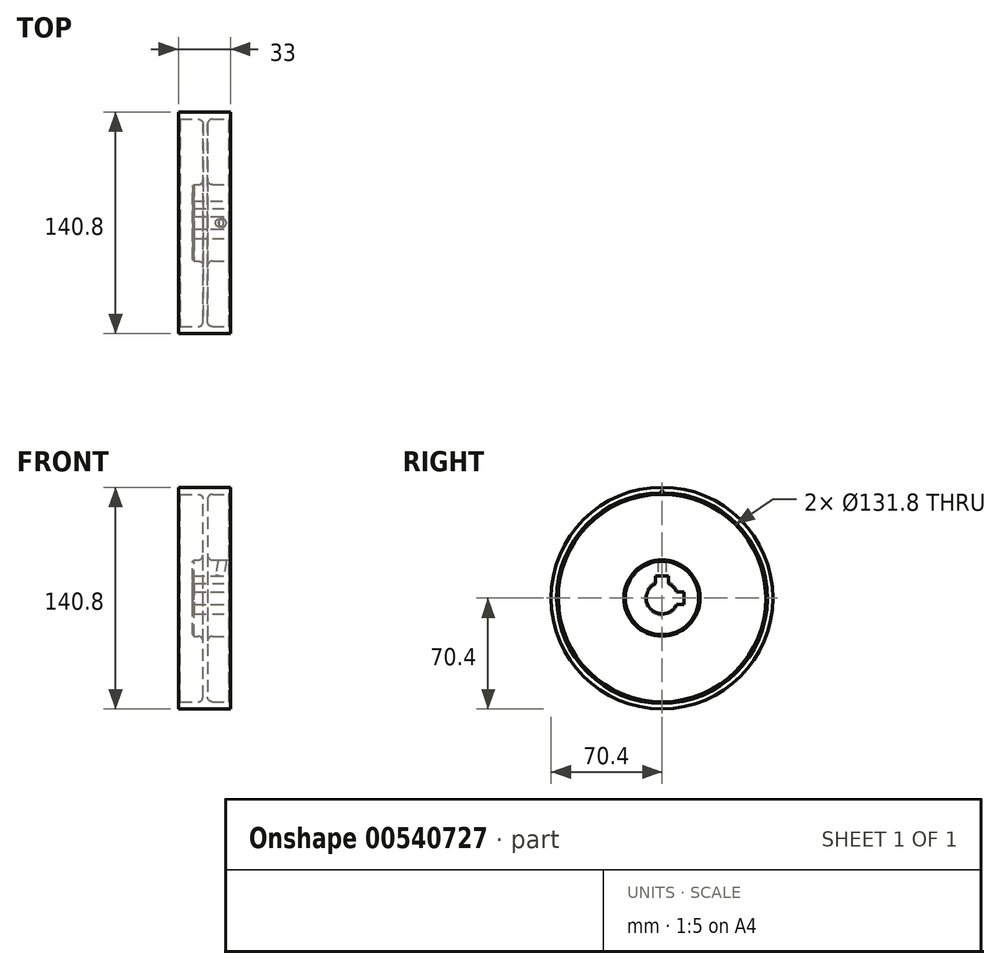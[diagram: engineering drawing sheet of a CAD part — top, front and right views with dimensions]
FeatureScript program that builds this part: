
annotation { "Feature Type Name" : "Feature", "Feature Type Description" : "" }
export const myFeature = defineFeature(function(context is Context, id is Id, definition is map)
    precondition{}
    {
        {
            var Q0;
            Q0=qCreatedBy(makeId("Front.planeOp"),FACE);
            var sketch = newSketch(context, id + "F0", { "sketchPlane" : qUnion([Q0])});
            skLineSegment(sketch, "E0", {"start": v(-11.99, 0) * mm, "end": v(-11.99, 24.25) * mm});
            skLineSegment(sketch, "E1", {"start": v(-11.99, 24.25) * mm, "end": v(-5.49, 24.25) * mm});
            skLineSegment(sketch, "E2", {"start": v(-5.49, 24.25) * mm, "end": v(-5.49, 65.9) * mm});
            skLineSegment(sketch, "E3", {"start": v(-5.49, 65.9) * mm, "end": v(-20.99, 65.9) * mm});
            skLineSegment(sketch, "E4", {"start": v(-20.99, 65.9) * mm, "end": v(-20.99, 70.4) * mm});
            skLineSegment(sketch, "E5", {"start": v(-20.99, 70.4) * mm, "end": v(12.01, 70.4) * mm});
            skLineSegment(sketch, "E6", {"start": v(12.01, 70.4) * mm, "end": v(12.01, 65.9) * mm});
            skLineSegment(sketch, "E7", {"start": v(12.01, 65.9) * mm, "end": v(-2.49, 65.9) * mm});
            skLineSegment(sketch, "E8", {"start": v(-2.49, 65.9) * mm, "end": v(-2.49, 24.25) * mm});
            skLineSegment(sketch, "E9", {"start": v(-2.49, 24.25) * mm, "end": v(12.01, 24.25) * mm});
            skLineSegment(sketch, "E10", {"start": v(12.01, 24.25) * mm, "end": v(12.01, 0) * mm});
            skLineSegment(sketch, "E11", {"start": v(0, 0) * mm, "end": v(-51.76, 0) * mm, "construction": true});
            skLineSegment(sketch, "E12", {"start": v(-11.99, 0) * mm, "end": v(12.01, 0) * mm});
            skSolve(sketch);
        }
        {
            var Q0;
            Q0=makeQuery(id+"F0.imprint","IMPRINT",FACE,{"disambiguationData":[TD([[makeQuery(id+"F0.imprint","IMPRINT",EDGE,{"derivedFrom":sQuery(id+"F0.wireOp",EDGE,"E0")}),-1.0]])]});
            var Q1;
            Q1=sQuery(id+"F0.wireOp",EDGE,"E11");
            revolve(context, id + "F1", {"surfaceOperationType" : NewSurfaceOperationType.NEW, "entities" : qUnion([Q0]), "axis" : qUnion([Q1]), "revolveType" : RevolveType.FULL});
        }
        {
            var Q0;
            Q0=makeQuery(id+"F1.opRevolve","SWEPT_EDGE",EDGE,{"disambiguationData":[OSD([sQuery(id+"F0.wireOp",EDGE,"E8"),sQuery(id+"F0.wireOp",EDGE,"E9")])]});
            var Q1;
            Q1=makeQuery(id+"F1.opRevolve","SWEPT_EDGE",EDGE,{"disambiguationData":[OSD([sQuery(id+"F0.wireOp",EDGE,"E7"),sQuery(id+"F0.wireOp",EDGE,"E8")])]});
            var Q2;
            Q2=makeQuery(id+"F1.opRevolve","SWEPT_EDGE",EDGE,{"disambiguationData":[OSD([sQuery(id+"F0.wireOp",EDGE,"E1"),sQuery(id+"F0.wireOp",EDGE,"E2")])]});
            var Q3;
            Q3=makeQuery(id+"F1.opRevolve","SWEPT_EDGE",EDGE,{"disambiguationData":[OSD([sQuery(id+"F0.wireOp",EDGE,"E2"),sQuery(id+"F0.wireOp",EDGE,"E3")])]});
            fillet(context, id + "F2", {"entities" : qUnion([Q0, Q1, Q2, Q3]), "radius" : 3 * mm, "tangentPropagation" : true, "allowEdgeOverflow" : false});
        }
        {
            var Q0;
            Q0=makeQuery(id+"F1.opRevolve","SWEPT_FACE",FACE,{"disambiguationData":[OSD([sQuery(id+"F0.wireOp",EDGE,"E10")])]});
            var sketch = newSketch(context, id + "F3", { "sketchPlane" : qUnion([Q0])});
            skArc(sketch, "E13", {"start": v(-4, 9.17) * mm, "mid": v(-7.07, -7.07) * mm, "end": v(9.17, -4) * mm});
            skLineSegment(sketch, "E14.bottom", {"start": v(4, 14) * mm, "end": v(-4, 14) * mm});
            skLineSegment(sketch, "E14.left", {"start": v(4, 14) * mm, "end": v(4, 9.17) * mm});
            skLineSegment(sketch, "E14.right", {"start": v(-4, 14) * mm, "end": v(-4, 9.17) * mm});
            skPoint(sketch, "E14.middle", {"position": v(0, 10) * mm});
            skLineSegment(sketch, "E15.bottom", {"start": v(14, -4) * mm, "end": v(9.17, -4) * mm});
            skLineSegment(sketch, "E15.top", {"start": v(14, 4) * mm, "end": v(9.17, 4) * mm});
            skLineSegment(sketch, "E15.left", {"start": v(14, -4) * mm, "end": v(14, 4) * mm});
            skPoint(sketch, "E15.middle", {"position": v(10, 0) * mm});
            skArc(sketch, "E16.trimOffspring", {"start": v(9.17, 4) * mm, "mid": v(7.07, 7.07) * mm, "end": v(4, 9.17) * mm});
            skSolve(sketch);
        }
        {
            var Q0;
            Q0=makeQuery(id+"F3.imprint","IMPRINT",FACE,{"disambiguationData":[TD([[makeQuery(id+"F3.imprint","IMPRINT",EDGE,{"derivedFrom":sQuery(id+"F3.wireOp",EDGE,"E13")}),1.0]])]});
            extrude(context, id + "F4", {"entities" : qUnion([Q0]), "operationType" : NewBodyOperationType.REMOVE, "oppositeDirection" : true, "depth" : 25 * mm, "offsetDistance" : 25 * mm});
        }
        {
            var Q0;
            Q0=makeQuery(id+"F1.opRevolve","SWEPT_EDGE",EDGE,{"disambiguationData":[OSD([sQuery(id+"F0.wireOp",EDGE,"E6"),sQuery(id+"F0.wireOp",EDGE,"E7")])]});
            var Q1;
            Q1=makeQuery(id+"F1.opRevolve","SWEPT_EDGE",EDGE,{"disambiguationData":[OSD([sQuery(id+"F0.wireOp",EDGE,"E9"),sQuery(id+"F0.wireOp",EDGE,"E10")])]});
            var Q2;
            Q2=makeQuery(id+"F4.boolean.opBoolean","COPY",EDGE,{"derivedFrom":makeQuery(id+"F4.opExtrude","CAP_EDGE",EDGE,{"disambiguationData":[OSD([sQuery(id+"F3.wireOp",EDGE,"E13")])],"isStart":true})});
            var Q3;
            Q3=makeQuery(id+"F4.boolean.opBoolean","COPY",EDGE,{"derivedFrom":makeQuery(id+"F4.opExtrude","CAP_EDGE",EDGE,{"disambiguationData":[OSD([sQuery(id+"F3.wireOp",EDGE,"E16.trimOffspring")])],"isStart":true})});
            var Q4;
            Q4=makeQuery(id+"F1.opRevolve","SWEPT_EDGE",EDGE,{"disambiguationData":[OSD([sQuery(id+"F0.wireOp",EDGE,"E0"),sQuery(id+"F0.wireOp",EDGE,"E1")])]});
            var Q5;
            Q5=makeQuery(id+"F1.opRevolve","SWEPT_EDGE",EDGE,{"disambiguationData":[OSD([sQuery(id+"F0.wireOp",EDGE,"E3"),sQuery(id+"F0.wireOp",EDGE,"E4")])]});
            var Q6;
            Q6=makeQuery(id+"F4.boolean.opBoolean","INTERSECT",EDGE,{"derivedFrom":[makeQuery(id+"F1.opRevolve","SWEPT_FACE",FACE,{"disambiguationData":[OSD([sQuery(id+"F0.wireOp",EDGE,"E0")])]}),makeQuery(id+"F4.opExtrude","SWEPT_FACE",FACE,{"disambiguationData":[OSD([sQuery(id+"F3.wireOp",EDGE,"E13")])]})]});
            var Q7;
            Q7=makeQuery(id+"F4.boolean.opBoolean","INTERSECT",EDGE,{"derivedFrom":[makeQuery(id+"F1.opRevolve","SWEPT_FACE",FACE,{"disambiguationData":[OSD([sQuery(id+"F0.wireOp",EDGE,"E0")])]}),makeQuery(id+"F4.opExtrude","SWEPT_FACE",FACE,{"disambiguationData":[OSD([sQuery(id+"F3.wireOp",EDGE,"E16.trimOffspring")])]})]});
            chamfer(context, id + "F5", {"entities" : qUnion([Q0, Q1, Q2, Q3, Q4, Q5, Q6, Q7]), "width" : 1 * mm, "tangentPropagation" : true});
        }
        {
            var Q0;
            Q0=qCreatedBy(makeId("Front.planeOp"),FACE);
            var sketch = newSketch(context, id + "F6", { "sketchPlane" : qUnion([Q0])});
            skLineSegment(sketch, "E17.0.0", {"start": v(-11.99, 14) * mm, "end": v(-11.99, 10.25) * mm, "construction": true});
            skFitSpline(sketch, "E17.0.1", {"points": [v(-11.99, 10.25) * mm, v(-11.65, 9.89) * mm, v(-11.32, 9.53) * mm, v(-10.99, 9.17) * mm], "construction": true});
            skLineSegment(sketch, "E17.0.2", {"start": v(-10.99, 9.17) * mm, "end": v(11.01, 9.17) * mm, "construction": true});
            skFitSpline(sketch, "E17.0.3", {"points": [v(11.01, 9.17) * mm, v(11.34, 9.53) * mm, v(11.68, 9.89) * mm, v(12.01, 10.25) * mm], "construction": true});
            skLineSegment(sketch, "E17.0.4", {"start": v(12.01, 10.25) * mm, "end": v(12.01, 14) * mm, "construction": true});
            skLineSegment(sketch, "E17.0.5", {"start": v(12.01, 14) * mm, "end": v(-11.99, 14) * mm, "construction": true});
            skLineSegment(sketch, "E18", {"start": v(5.12, 14) * mm, "end": v(13.88, 63.66) * mm, "construction": true});
            skSolve(sketch);
        }
        {
            var Q0;
            Q0=sQuery(id+"F6.wireOp",VERTEX,"E18.start");
            var Q1;
            Q1=sQuery(id+"F6.wireOp",EDGE,"E18");
            cPlane(context, id + "F7", {"entities" : qUnion([Q0, Q1]), "cplaneType" : CPlaneType.LINE_POINT, "offset" : 25 * mm, "width" : 150 * mm, "height" : 150 * mm});
        }
        {
            var Q0;
            Q0=qCreatedBy(id+"F7.planeOp",FACE);
            var sketch = newSketch(context, id + "F8", { "sketchPlane" : qUnion([Q0])});
            skCircle(sketch, "E19", {"center": v(2.53, 0) * mm, "radius": 5.8 * mm});
            skSolve(sketch);
        }
        {
            var Q0;
            Q0=sQuery(id+"F8.wireOp",VERTEX,"E19.center");
            var Q1;
            Q1=makeQuery(id+"F1.opRevolve","SWEPT_BODY",BODY,{"disambiguationData":[OSD([sQuery(id+"F0.wireOp",EDGE,"E0"),sQuery(id+"F0.wireOp",EDGE,"E1"),sQuery(id+"F0.wireOp",EDGE,"E2"),sQuery(id+"F0.wireOp",EDGE,"E3"),sQuery(id+"F0.wireOp",EDGE,"E4"),sQuery(id+"F0.wireOp",EDGE,"E5"),sQuery(id+"F0.wireOp",EDGE,"E6"),sQuery(id+"F0.wireOp",EDGE,"E7"),sQuery(id+"F0.wireOp",EDGE,"E8"),sQuery(id+"F0.wireOp",EDGE,"E9"),sQuery(id+"F0.wireOp",EDGE,"E10"),sQuery(id+"F0.wireOp",EDGE,"E12")])]});
            hole(context, id + "F9", {"style" : HoleStyle.SIMPLE, "endStyle" : HoleEndStyle.THROUGH, "oppositeDirection" : true, "standardTappedOrClearance" : lookupTablePath({ "standard" : "ANSI", "engagement" : "75%", "pitch" : "20 tpi", "size" : "1/4", "type" : "Tapped" }), "standardBlindInLast" : lookupTablePath({ "standard" : "ANSI", "engagement" : "75%", "pitch" : "20 tpi", "size" : "1/4", "type" : "Tapped" }), "holeDiameter" : 5.1 * mm, "majorDiameter" : 6.35 * mm, "showTappedDepth" : true, "isTappedThrough" : true, "tappedDepth" : 12 * mm, "tapClearance" : 3, "locations" : qUnion([Q0]), "scope" : qUnion([Q1])});
        }
    });
